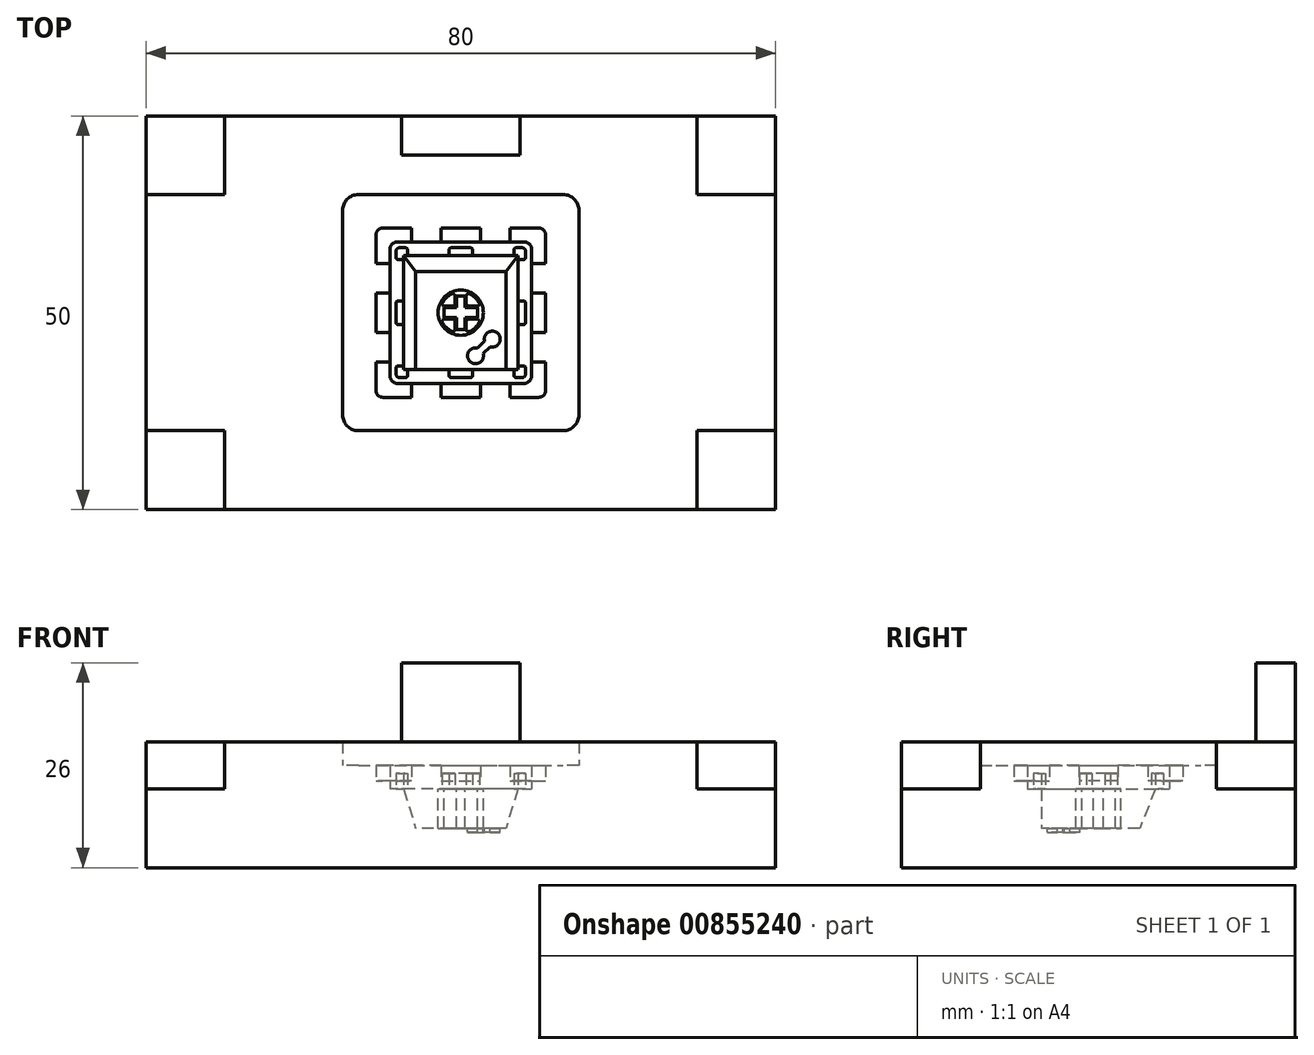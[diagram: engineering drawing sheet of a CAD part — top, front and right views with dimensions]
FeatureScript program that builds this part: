
annotation { "Feature Type Name" : "Feature", "Feature Type Description" : "" }
export const myFeature = defineFeature(function(context is Context, id is Id, definition is map)
    precondition{}
    {
        {
            var Q0;
            Q0=qCreatedBy(makeId("Top.planeOp"),FACE);
            var sketch = newSketch(context, id + "F0", { "sketchPlane" : qUnion([Q0])});
            skLineSegment(sketch, "E0", {"start": v(40, -25) * mm, "end": v(-40, -25) * mm});
            skLineSegment(sketch, "E1", {"start": v(-40, -25) * mm, "end": v(-40, 25) * mm});
            skLineSegment(sketch, "E2", {"start": v(-40, 25) * mm, "end": v(40, 25) * mm});
            skLineSegment(sketch, "E3", {"start": v(40, 25) * mm, "end": v(40, -25) * mm});
            skSolve(sketch);
        }
        {
            var Q0;
            Q0=makeQuery(id+"F0.imprint","IMPRINT",FACE,{"disambiguationData":[TD([[makeQuery(id+"F0.imprint","IMPRINT",EDGE,{"derivedFrom":sQuery(id+"F0.wireOp",EDGE,"E0")}),-1.0]])]});
            extrude(context, id + "F1", {"entities" : qUnion([Q0]), "depth" : 10 * mm, "offsetDistance" : 25 * mm});
        }
        {
            var Q0;
            Q0=qCreatedBy(makeId("Top.planeOp"),FACE);
            var sketch = newSketch(context, id + "F2", { "sketchPlane" : qUnion([Q0])});
            skCircle(sketch, "E4", {"center": v(0, 0) * mm, "radius": 2.87 * mm});
            skLineSegment(sketch, "E5", {"start": v(2.12, -0.64) * mm, "end": v(0.54, -0.64) * mm});
            skLineSegment(sketch, "E6", {"start": v(-2.12, 0.64) * mm, "end": v(-0.54, 0.64) * mm});
            skLineSegment(sketch, "E7", {"start": v(-0.54, 2.13) * mm, "end": v(-0.54, 0.64) * mm});
            skLineSegment(sketch, "E8", {"start": v(0.54, 2.12) * mm, "end": v(0.54, 0.64) * mm});
            skLineSegment(sketch, "E9.trimOffspring", {"start": v(-0.54, -0.64) * mm, "end": v(-0.54, -2.12) * mm});
            skLineSegment(sketch, "E10.trimOffspring", {"start": v(0.54, -0.64) * mm, "end": v(0.54, -2.13) * mm});
            skLineSegment(sketch, "E11.trimOffspring", {"start": v(0.54, 0.64) * mm, "end": v(2.12, 0.64) * mm});
            skLineSegment(sketch, "E12.trimOffspring", {"start": v(-0.54, -0.64) * mm, "end": v(-2.13, -0.64) * mm});
            skLineSegment(sketch, "E13", {"start": v(-7.25, -7.25) * mm, "end": v(7.25, -7.25) * mm});
            skLineSegment(sketch, "E14", {"start": v(7.25, -7.25) * mm, "end": v(7.25, 7.25) * mm});
            skLineSegment(sketch, "E15", {"start": v(7.25, 7.25) * mm, "end": v(-7.25, 7.25) * mm});
            skLineSegment(sketch, "E16", {"start": v(-5.75, -7.25) * mm, "end": v(5.75, -7.25) * mm});
            skLineSegment(sketch, "E17", {"start": v(5.75, 5.25) * mm, "end": v(-5.75, 5.25) * mm});
            skLineSegment(sketch, "E18", {"start": v(-7.25, 7.25) * mm, "end": v(-7.25, -7.25) * mm});
            skLineSegment(sketch, "E19", {"start": v(-5.75, 5.25) * mm, "end": v(-5.75, -7.25) * mm});
            skLineSegment(sketch, "E20", {"start": v(5.75, 5.25) * mm, "end": v(5.75, -7.25) * mm});
            skLineSegment(sketch, "E21", {"start": v(-2.13, 0.64) * mm, "end": v(-2.13, -0.64) * mm});
            skLineSegment(sketch, "E22", {"start": v(-0.54, 2.13) * mm, "end": v(0.54, 2.12) * mm});
            skLineSegment(sketch, "E23", {"start": v(2.13, 0.64) * mm, "end": v(2.12, -0.64) * mm});
            skLineSegment(sketch, "E24", {"start": v(-0.54, -2.12) * mm, "end": v(0.54, -2.13) * mm});
            skSolve(sketch);
        }
        {
            var Q0;
            Q0=qCreatedBy(makeId("Top.planeOp"),FACE);
            cPlane(context, id + "F3", {"entities" : qUnion([Q0]), "cplaneType" : CPlaneType.OFFSET, "offset" : 5 * mm, "width" : 150 * mm, "height" : 150 * mm});
        }
        {
            var Q0;
            Q0=qCreatedBy(id+"F3.planeOp",FACE);
            var sketch = newSketch(context, id + "F4", { "sketchPlane" : qUnion([Q0])});
            skLineSegment(sketch, "E25.0", {"start": v(5.75, 5.25) * mm, "end": v(-5.75, 5.25) * mm});
            skLineSegment(sketch, "E25.1", {"start": v(-5.75, 5.25) * mm, "end": v(-5.75, -7.25) * mm});
            skLineSegment(sketch, "E25.2", {"start": v(-5.75, -7.25) * mm, "end": v(5.75, -7.25) * mm});
            skLineSegment(sketch, "E25.3", {"start": v(5.75, 5.25) * mm, "end": v(5.75, -7.25) * mm});
            skSolve(sketch);
        }
        {
            var Q0;
            Q0=qCreatedBy(makeId("Top.planeOp"),FACE);
            var sketch = newSketch(context, id + "F5", { "sketchPlane" : qUnion([Q0])});
            skLineSegment(sketch, "E26.0", {"start": v(7.25, 7.25) * mm, "end": v(-7.25, 7.25) * mm});
            skLineSegment(sketch, "E26.1", {"start": v(-7.25, 7.25) * mm, "end": v(-7.25, -7.25) * mm});
            skLineSegment(sketch, "E26.2", {"start": v(-7.25, -7.25) * mm, "end": v(7.25, -7.25) * mm});
            skLineSegment(sketch, "E26.3", {"start": v(7.25, -7.25) * mm, "end": v(7.25, 7.25) * mm});
            skSolve(sketch);
        }
        {
            var Q0;
            Q0 = qSketchRegion(id + "F5", true);
            var Q1;
            Q1=makeQuery(id+"F4.imprint","IMPRINT",FACE,{"disambiguationData":[TD([[makeQuery(id+"F4.imprint","IMPRINT",EDGE,{"derivedFrom":sQuery(id+"F4.wireOp",EDGE,"E25.0")}),1.0]])]});
            loft(context, id + "F6", {"operationType" : NewBodyOperationType.REMOVE, "sheetProfilesArray" : [{ "sheetProfileEntities" : qUnion([Q0]) }, { "sheetProfileEntities" : qUnion([Q1]) }]});
        }
        {
            var Q0;
            Q0=makeQuery(id+"F2.imprint","IMPRINT",FACE,{"disambiguationData":[TD([[makeQuery(id+"F2.imprint","IMPRINT",EDGE,{"derivedFrom":sQuery(id+"F2.wireOp",EDGE,"E4")}),1.0]])]});
            extrude(context, id + "F7", {"entities" : qUnion([Q0]), "operationType" : NewBodyOperationType.ADD, "depth" : 5 * mm, "offsetDistance" : 25 * mm});
        }
        {
            var Q0;
            Q0=makeQuery(id+"F0.imprint","IMPRINT",FACE,{"disambiguationData":[TD([[makeQuery(id+"F0.imprint","IMPRINT",EDGE,{"derivedFrom":sQuery(id+"F0.wireOp",EDGE,"E0")}),-1.0]])]});
            var sketch = newSketch(context, id + "F8", { "sketchPlane" : qUnion([Q0])});
            skLineSegment(sketch, "E27", {"start": v(8, 9) * mm, "end": v(-8, 9) * mm});
            skLineSegment(sketch, "E28", {"start": v(-9, 8) * mm, "end": v(-9, -8) * mm});
            skLineSegment(sketch, "E29", {"start": v(-8, -9) * mm, "end": v(8, -9) * mm});
            skLineSegment(sketch, "E30", {"start": v(9, -8) * mm, "end": v(9, 8) * mm});
            skLineSegment(sketch, "E31", {"start": v(13, -15) * mm, "end": v(-13, -15) * mm});
            skLineSegment(sketch, "E32", {"start": v(-15, -13) * mm, "end": v(-15, 13) * mm});
            skLineSegment(sketch, "E33", {"start": v(-13, 15) * mm, "end": v(13, 15) * mm});
            skLineSegment(sketch, "E34", {"start": v(15, 13) * mm, "end": v(15, -13) * mm});
            skPoint(sketch, "E35.visualSharp", {"position": v(-15, -15) * mm});
            skArc(sketch, "E35.filletArc", {"start": v(-15, -13) * mm, "mid": v(-14.41, -14.41) * mm, "end": v(-13, -15) * mm});
            skPoint(sketch, "E36.visualSharp", {"position": v(15, -15) * mm});
            skArc(sketch, "E36.filletArc", {"start": v(13, -15) * mm, "mid": v(14.41, -14.41) * mm, "end": v(15, -13) * mm});
            skPoint(sketch, "E37.visualSharp", {"position": v(15, 15) * mm});
            skArc(sketch, "E37.filletArc", {"start": v(15, 13) * mm, "mid": v(14.41, 14.41) * mm, "end": v(13, 15) * mm});
            skPoint(sketch, "E38.visualSharp", {"position": v(-15, 15) * mm});
            skArc(sketch, "E38.filletArc", {"start": v(-13, 15) * mm, "mid": v(-14.41, 14.41) * mm, "end": v(-15, 13) * mm});
            skLineSegment(sketch, "E39", {"start": v(-7.5, 20) * mm, "end": v(-7.5, 25) * mm});
            skLineSegment(sketch, "E40", {"start": v(-7.5, 25) * mm, "end": v(7.5, 25) * mm});
            skLineSegment(sketch, "E41", {"start": v(7.5, 25) * mm, "end": v(7.5, 20) * mm});
            skLineSegment(sketch, "E42", {"start": v(-7.5, 20) * mm, "end": v(7.5, 20) * mm});
            skLineSegment(sketch, "E43.0", {"start": v(-40, -25) * mm, "end": v(-40, 25) * mm});
            skLineSegment(sketch, "E43.1", {"start": v(40, -25) * mm, "end": v(-40, -25) * mm});
            skLineSegment(sketch, "E43.2", {"start": v(40, 25) * mm, "end": v(40, -25) * mm});
            skLineSegment(sketch, "E43.3", {"start": v(-40, 25) * mm, "end": v(40, 25) * mm});
            skLineSegment(sketch, "E44", {"start": v(-40, -25) * mm, "end": v(-40, -15) * mm});
            skLineSegment(sketch, "E45", {"start": v(-40, -15) * mm, "end": v(-30, -15) * mm});
            skLineSegment(sketch, "E46", {"start": v(-30, -15) * mm, "end": v(-30, -25) * mm});
            skLineSegment(sketch, "E47", {"start": v(-30, -25) * mm, "end": v(-40, -25) * mm});
            skLineSegment(sketch, "E48", {"start": v(40, -25) * mm, "end": v(30, -25) * mm});
            skLineSegment(sketch, "E49", {"start": v(30, -25) * mm, "end": v(30, -15) * mm});
            skLineSegment(sketch, "E50", {"start": v(30, -15) * mm, "end": v(40, -15) * mm});
            skLineSegment(sketch, "E51", {"start": v(40, -15) * mm, "end": v(40, -25) * mm});
            skLineSegment(sketch, "E52", {"start": v(-40, 25) * mm, "end": v(-40, 15) * mm});
            skLineSegment(sketch, "E53", {"start": v(-40, 15) * mm, "end": v(-30, 15) * mm});
            skLineSegment(sketch, "E54", {"start": v(-30, 15) * mm, "end": v(-30, 25) * mm});
            skLineSegment(sketch, "E55", {"start": v(-30, 25) * mm, "end": v(-40, 25) * mm});
            skLineSegment(sketch, "E56", {"start": v(40, 25) * mm, "end": v(40, 15) * mm});
            skLineSegment(sketch, "E57", {"start": v(40, 15) * mm, "end": v(30, 15) * mm});
            skLineSegment(sketch, "E58", {"start": v(30, 15) * mm, "end": v(30, 25) * mm});
            skLineSegment(sketch, "E59", {"start": v(30, 25) * mm, "end": v(40, 25) * mm});
            skPoint(sketch, "E60.visualSharp", {"position": v(-9, 9) * mm});
            skArc(sketch, "E60.filletArc", {"start": v(-8, 9) * mm, "mid": v(-8.7, 8.7) * mm, "end": v(-9, 8) * mm});
            skPoint(sketch, "E61.visualSharp", {"position": v(9, 9) * mm});
            skArc(sketch, "E61.filletArc", {"start": v(9, 8) * mm, "mid": v(8.7, 8.7) * mm, "end": v(8, 9) * mm});
            skPoint(sketch, "E62.visualSharp", {"position": v(9, -9) * mm});
            skArc(sketch, "E62.filletArc", {"start": v(8, -9) * mm, "mid": v(8.7, -8.7) * mm, "end": v(9, -8) * mm});
            skPoint(sketch, "E63.visualSharp", {"position": v(-9, -9) * mm});
            skArc(sketch, "E63.filletArc", {"start": v(-9, -8) * mm, "mid": v(-8.7, -8.7) * mm, "end": v(-8, -9) * mm});
            skSolve(sketch);
        }
        {
            var Q0;
            Q0=makeQuery(id+"F8.imprint","IMPRINT",FACE,{"disambiguationData":[TD([[makeQuery(id+"F8.imprint","IMPRINT",EDGE,{"derivedFrom":sQuery(id+"F8.wireOp",EDGE,"E27")}),-1.0]])]});
            var Q1;
            Q1=makeQuery(id+"F8.imprint","IMPRINT",FACE,{"disambiguationData":[TD([[makeQuery(id+"F8.imprint","IMPRINT",EDGE,{"derivedFrom":sQuery(id+"F8.wireOp",EDGE,"E48")}),-1.0]])]});
            var Q2;
            Q2=makeQuery(id+"F8.imprint","IMPRINT",FACE,{"disambiguationData":[TD([[makeQuery(id+"F8.imprint","IMPRINT",EDGE,{"derivedFrom":sQuery(id+"F8.wireOp",EDGE,"E56")}),-1.0]])]});
            var Q3;
            Q3=makeQuery(id+"F8.imprint","IMPRINT",FACE,{"disambiguationData":[TD([[makeQuery(id+"F8.imprint","IMPRINT",EDGE,{"derivedFrom":sQuery(id+"F8.wireOp",EDGE,"E31")}),1.0]])]});
            var Q4;
            {var subQ0=sQuery(id+"F8.wireOp",EDGE,"E39");Q4=makeQuery(id+"F8.imprint","IMPRINT",FACE,{"disambiguationData":[TD([[makeQuery(id+"F8.imprint","IMPRINT",EDGE,{"derivedFrom":subQ0}),-1.0]])]});}
            var Q5;
            Q5=makeQuery(id+"F8.imprint","IMPRINT",FACE,{"disambiguationData":[TD([[makeQuery(id+"F8.imprint","IMPRINT",EDGE,{"derivedFrom":sQuery(id+"F8.wireOp",EDGE,"E52")}),-1.0]])]});
            var Q6;
            Q6=makeQuery(id+"F8.imprint","IMPRINT",FACE,{"disambiguationData":[TD([[makeQuery(id+"F8.imprint","IMPRINT",EDGE,{"derivedFrom":sQuery(id+"F8.wireOp",EDGE,"E44")}),-1.0]])]});
            extrude(context, id + "F9", {"entities" : qUnion([Q0, Q1, Q2, Q3, Q4, Q5, Q6]), "operationType" : NewBodyOperationType.ADD, "oppositeDirection" : true, "depth" : 3 * mm, "offsetDistance" : 25 * mm});
        }
        {
            var Q0;
            Q0=makeQuery(id+"F8.imprint","IMPRINT",FACE,{"disambiguationData":[TD([[makeQuery(id+"F8.imprint","IMPRINT",EDGE,{"derivedFrom":sQuery(id+"F8.wireOp",EDGE,"E31")}),1.0]])]});
            var Q1;
            Q1=makeQuery(id+"F8.imprint","IMPRINT",FACE,{"disambiguationData":[TD([[makeQuery(id+"F8.imprint","IMPRINT",EDGE,{"derivedFrom":sQuery(id+"F8.wireOp",EDGE,"E48")}),-1.0]])]});
            var Q2;
            Q2=makeQuery(id+"F8.imprint","IMPRINT",FACE,{"disambiguationData":[TD([[makeQuery(id+"F8.imprint","IMPRINT",EDGE,{"derivedFrom":sQuery(id+"F8.wireOp",EDGE,"E56")}),-1.0]])]});
            var Q3;
            Q3=makeQuery(id+"F8.imprint","IMPRINT",FACE,{"disambiguationData":[TD([[makeQuery(id+"F8.imprint","IMPRINT",EDGE,{"derivedFrom":sQuery(id+"F8.wireOp",EDGE,"E52")}),-1.0]])]});
            var Q4;
            {var subQ0=sQuery(id+"F8.wireOp",EDGE,"E39");Q4=makeQuery(id+"F8.imprint","IMPRINT",FACE,{"disambiguationData":[TD([[makeQuery(id+"F8.imprint","IMPRINT",EDGE,{"derivedFrom":subQ0}),-1.0]])]});}
            var Q5;
            Q5=makeQuery(id+"F8.imprint","IMPRINT",FACE,{"disambiguationData":[TD([[makeQuery(id+"F8.imprint","IMPRINT",EDGE,{"derivedFrom":sQuery(id+"F8.wireOp",EDGE,"E44")}),-1.0]])]});
            extrude(context, id + "F10", {"entities" : qUnion([Q0, Q1, Q2, Q3, Q4, Q5]), "operationType" : NewBodyOperationType.ADD, "oppositeDirection" : true, "depth" : 6 * mm, "offsetDistance" : 25 * mm});
        }
        {
            var Q0;
            Q0=qCreatedBy(id+"F3.planeOp",FACE);
            var sketch = newSketch(context, id + "F11", { "sketchPlane" : qUnion([Q0])});
            skFitSpline(sketch, "E64", {"points": [v(-4, -5.85) * mm, v(-3.95, -6) * mm, v(-3.67, -6.34) * mm, v(-3.46, -6.52) * mm, v(-3.17, -6.5) * mm, v(-2.96, -6.4) * mm, v(-2.55, -6.17) * mm, v(-2.35, -5.86) * mm, v(-2.28, -5.34) * mm, v(-2.43, -4.96) * mm, v(-2.58, -4.76) * mm, v(-2.67, -4.7) * mm, v(-2.69, -4.64) * mm, v(-2.62, -4.54) * mm, v(-2.33, -4.48) * mm, v(-2.15, -4.64) * mm, v(-1.78, -4.82) * mm, v(-1.4, -4.65) * mm, v(-1.35, -4.47) * mm, v(-1.26, -4.08) * mm, v(-1.33, -3.65) * mm, v(-1.64, -3.19) * mm, v(-2.13, -2.87) * mm, v(-3.35, -2.7) * mm, v(-4.24, -2.79) * mm, v(-4.63, -3.02) * mm, v(-4.9, -3.3) * mm, v(-4.95, -3.8) * mm, v(-4.7, -4.22) * mm, v(-4.4, -4.5) * mm, v(-4.15, -4.7) * mm, v(-4.06, -4.83) * mm, v(-4.1, -5.06) * mm, v(-4.22, -5.17) * mm, v(-4.39, -5.14) * mm, v(-4.57, -5.22) * mm, v(-4.46, -5.43) * mm, v(-4.55, -5.55) * mm, v(-4.61, -5.66) * mm, v(-4.6, -5.86) * mm, v(-4.48, -5.95) * mm, v(-4.31, -5.9) * mm, v(-4.16, -5.85) * mm, v(-4, -5.85) * mm]});
            skSolve(sketch);
        }
        {
            var Q0;
            Q0=makeQuery(id+"F10.opExtrude","CAP_FACE",FACE,{"disambiguationData":[OSD([sQuery(id+"F8.wireOp",EDGE,"E31"),sQuery(id+"F8.wireOp",EDGE,"E32"),sQuery(id+"F8.wireOp",EDGE,"E33"),sQuery(id+"F8.wireOp",EDGE,"E34"),sQuery(id+"F8.wireOp",EDGE,"E35.filletArc"),sQuery(id+"F8.wireOp",EDGE,"E36.filletArc"),sQuery(id+"F8.wireOp",EDGE,"E37.filletArc"),sQuery(id+"F8.wireOp",EDGE,"E38.filletArc"),sQuery(id+"F8.wireOp",EDGE,"E43.0"),sQuery(id+"F8.wireOp",EDGE,"E43.1"),sQuery(id+"F8.wireOp",EDGE,"E43.2"),sQuery(id+"F8.wireOp",EDGE,"E43.3"),sQuery(id+"F8.wireOp",EDGE,"E44"),sQuery(id+"F8.wireOp",EDGE,"E47"),sQuery(id+"F8.wireOp",EDGE,"E48"),sQuery(id+"F8.wireOp",EDGE,"E51"),sQuery(id+"F8.wireOp",EDGE,"E52"),sQuery(id+"F8.wireOp",EDGE,"E55"),sQuery(id+"F8.wireOp",EDGE,"E56"),sQuery(id+"F8.wireOp",EDGE,"E59")])],"isStart":false});
            var sketch = newSketch(context, id + "F12", { "sketchPlane" : qUnion([Q0])});
            skLineSegment(sketch, "E65.0", {"start": v(40, 25) * mm, "end": v(-40, 25) * mm});
            skLineSegment(sketch, "E65.1", {"start": v(40, -25) * mm, "end": v(40, 25) * mm});
            skLineSegment(sketch, "E65.2", {"start": v(-40, -25) * mm, "end": v(40, -25) * mm});
            skLineSegment(sketch, "E65.3", {"start": v(-40, 25) * mm, "end": v(-40, -25) * mm});
            skLineSegment(sketch, "E66", {"start": v(-40, -25) * mm, "end": v(-40, -20) * mm});
            skLineSegment(sketch, "E67", {"start": v(-40, -20) * mm, "end": v(-35, -20) * mm});
            skLineSegment(sketch, "E68", {"start": v(-35, -20) * mm, "end": v(-35, -25) * mm});
            skLineSegment(sketch, "E69", {"start": v(-35, -25) * mm, "end": v(-40, -25) * mm});
            skLineSegment(sketch, "E70", {"start": v(40, -25) * mm, "end": v(40, -20) * mm});
            skLineSegment(sketch, "E71", {"start": v(40, -20) * mm, "end": v(35, -20) * mm});
            skLineSegment(sketch, "E72", {"start": v(35, -20) * mm, "end": v(35, -25) * mm});
            skLineSegment(sketch, "E73", {"start": v(35, -25) * mm, "end": v(40, -25) * mm});
            skLineSegment(sketch, "E74", {"start": v(40, 25) * mm, "end": v(35, 25) * mm});
            skLineSegment(sketch, "E75", {"start": v(35, 25) * mm, "end": v(35, 20) * mm});
            skLineSegment(sketch, "E76", {"start": v(35, 20) * mm, "end": v(40, 20) * mm});
            skLineSegment(sketch, "E77", {"start": v(40, 20) * mm, "end": v(40, 25) * mm});
            skLineSegment(sketch, "E78", {"start": v(-40, 25) * mm, "end": v(-35, 25) * mm});
            skLineSegment(sketch, "E79", {"start": v(-35, 25) * mm, "end": v(-35, 20) * mm});
            skLineSegment(sketch, "E80", {"start": v(-35, 20) * mm, "end": v(-40, 20) * mm});
            skLineSegment(sketch, "E81", {"start": v(-40, 20) * mm, "end": v(-40, 25) * mm});
            skLineSegment(sketch, "E82", {"start": v(0, -20) * mm, "end": v(7.5, -20) * mm});
            skLineSegment(sketch, "E83", {"start": v(7.5, -20) * mm, "end": v(7.5, -25) * mm});
            skLineSegment(sketch, "E84", {"start": v(7.5, -25) * mm, "end": v(-7.5, -25) * mm});
            skLineSegment(sketch, "E85", {"start": v(-7.5, -25) * mm, "end": v(-7.5, -20) * mm});
            skLineSegment(sketch, "E86", {"start": v(-7.5, -20) * mm, "end": v(0, -20) * mm});
            skSolve(sketch);
        }
        {
            var Q0;
            Q0=makeQuery(id+"F12.imprint","IMPRINT",FACE,{"disambiguationData":[TD([[makeQuery(id+"F12.imprint","IMPRINT",EDGE,{"derivedFrom":sQuery(id+"F12.wireOp",EDGE,"E78")}),1.0]])]});
            var Q1;
            Q1=makeQuery(id+"F12.imprint","IMPRINT",FACE,{"disambiguationData":[TD([[makeQuery(id+"F12.imprint","IMPRINT",EDGE,{"derivedFrom":sQuery(id+"F12.wireOp",EDGE,"E74")}),1.0]])]});
            var Q2;
            Q2=makeQuery(id+"F12.imprint","IMPRINT",FACE,{"disambiguationData":[TD([[makeQuery(id+"F12.imprint","IMPRINT",EDGE,{"derivedFrom":sQuery(id+"F12.wireOp",EDGE,"E70")}),1.0]])]});
            var Q3;
            Q3=makeQuery(id+"F12.imprint","IMPRINT",FACE,{"disambiguationData":[TD([[makeQuery(id+"F12.imprint","IMPRINT",EDGE,{"derivedFrom":sQuery(id+"F12.wireOp",EDGE,"E82")}),-1.0]])]});
            var Q4;
            Q4=makeQuery(id+"F12.imprint","IMPRINT",FACE,{"disambiguationData":[TD([[makeQuery(id+"F12.imprint","IMPRINT",EDGE,{"derivedFrom":sQuery(id+"F12.wireOp",EDGE,"E66")}),1.0]])]});
            extrude(context, id + "F13", {"entities" : qUnion([Q0, Q1, Q2, Q3, Q4]), "operationType" : NewBodyOperationType.ADD, "depth" : 10 * mm, "offsetDistance" : 25 * mm});
        }
        {
            var Q0;
            Q0=makeQuery(id+"F1.opExtrude","CAP_FACE",FACE,{"disambiguationData":[OSD([sQuery(id+"F0.wireOp",EDGE,"E0"),sQuery(id+"F0.wireOp",EDGE,"E1"),sQuery(id+"F0.wireOp",EDGE,"E2"),sQuery(id+"F0.wireOp",EDGE,"E3")])],"isStart":true});
            var sketch = newSketch(context, id + "F14", { "sketchPlane" : qUnion([Q0])});
            skArc(sketch, "E87", {"start": v(-2.32, -1.27) * mm, "mid": v(-1.81, -1.93) * mm, "end": v(-1.12, -2.4) * mm});
            skLineSegment(sketch, "E88", {"start": v(-0.7, -2.13) * mm, "end": v(-0.7, -1.13) * mm});
            skLineSegment(sketch, "E89", {"start": v(0.73, 2.11) * mm, "end": v(0.73, 1.11) * mm});
            skLineSegment(sketch, "E90", {"start": v(2.07, 0.81) * mm, "end": v(1.03, 0.81) * mm});
            skLineSegment(sketch, "E91", {"start": v(2.06, -0.83) * mm, "end": v(1.03, -0.83) * mm});
            skLineSegment(sketch, "E92.trimOffspring", {"start": v(-1, 0.81) * mm, "end": v(-2.07, 0.81) * mm});
            skLineSegment(sketch, "E93.trimOffspring", {"start": v(-0.7, 1.11) * mm, "end": v(-0.7, 2.13) * mm});
            skLineSegment(sketch, "E94.trimOffspring", {"start": v(-1, -0.83) * mm, "end": v(-2.06, -0.83) * mm});
            skLineSegment(sketch, "E95.trimOffspring", {"start": v(0.73, -1.13) * mm, "end": v(0.73, -2.11) * mm});
            skArc(sketch, "E96.trimOffspring", {"start": v(2.33, 1.25) * mm, "mid": v(1.84, 1.9) * mm, "end": v(1.16, 2.38) * mm});
            skArc(sketch, "E97.trimOffspring", {"start": v(-1.12, 2.4) * mm, "mid": v(-1.82, 1.92) * mm, "end": v(-2.33, 1.25) * mm});
            skArc(sketch, "E98.trimOffspring", {"start": v(1.16, -2.38) * mm, "mid": v(1.83, -1.92) * mm, "end": v(2.32, -1.27) * mm});
            skLineSegment(sketch, "E99", {"start": v(1.2, 7.25) * mm, "end": v(-1.2, 7.25) * mm});
            skLineSegment(sketch, "E100", {"start": v(-1.5, 7.55) * mm, "end": v(-1.5, 7.95) * mm});
            skLineSegment(sketch, "E101", {"start": v(-1.2, 8.25) * mm, "end": v(1.2, 8.25) * mm});
            skLineSegment(sketch, "E102", {"start": v(1.5, 7.95) * mm, "end": v(1.5, 7.55) * mm});
            skLineSegment(sketch, "E103.MirrorCS", {"start": v(1.5, -7.95) * mm, "end": v(1.5, -7.55) * mm});
            skLineSegment(sketch, "E104.MirrorCS", {"start": v(-1.2, -8.25) * mm, "end": v(1.2, -8.25) * mm});
            skLineSegment(sketch, "E105.MirrorCS", {"start": v(1.2, -7.25) * mm, "end": v(-1.2, -7.25) * mm});
            skLineSegment(sketch, "E106.MirrorCS", {"start": v(-1.5, -7.55) * mm, "end": v(-1.5, -7.95) * mm});
            skLineSegment(sketch, "E107", {"start": v(-7.25, 1.2) * mm, "end": v(-7.25, -1.2) * mm});
            skLineSegment(sketch, "E108", {"start": v(-7.55, -1.5) * mm, "end": v(-7.95, -1.5) * mm});
            skLineSegment(sketch, "E109", {"start": v(-8.25, -1.2) * mm, "end": v(-8.25, 1.2) * mm});
            skLineSegment(sketch, "E110", {"start": v(-7.95, 1.5) * mm, "end": v(-7.55, 1.5) * mm});
            skLineSegment(sketch, "E111.MirrorCS", {"start": v(8.25, -1.2) * mm, "end": v(8.25, 1.2) * mm});
            skLineSegment(sketch, "E112.MirrorCS", {"start": v(7.55, -1.5) * mm, "end": v(7.95, -1.5) * mm});
            skLineSegment(sketch, "E113.MirrorCS", {"start": v(7.95, 1.5) * mm, "end": v(7.55, 1.5) * mm});
            skLineSegment(sketch, "E114.MirrorCS", {"start": v(7.25, 1.2) * mm, "end": v(7.25, -1.2) * mm});
            skLineSegment(sketch, "E115", {"start": v(8.25, -7.25) * mm, "end": v(8.25, -7.75) * mm});
            skLineSegment(sketch, "E116", {"start": v(7.75, -8.25) * mm, "end": v(7.25, -8.25) * mm});
            skLineSegment(sketch, "E117", {"start": v(7.25, -8.25) * mm, "end": v(7.05, -8.25) * mm});
            skLineSegment(sketch, "E118", {"start": v(6.75, -7.95) * mm, "end": v(6.75, -7.55) * mm});
            skLineSegment(sketch, "E119", {"start": v(7.05, -7.25) * mm, "end": v(7.25, -7.25) * mm});
            skLineSegment(sketch, "E120", {"start": v(8.25, -7.25) * mm, "end": v(8.25, -7.05) * mm});
            skLineSegment(sketch, "E121", {"start": v(7.95, -6.75) * mm, "end": v(7.55, -6.75) * mm});
            skLineSegment(sketch, "E122", {"start": v(7.25, -7.05) * mm, "end": v(7.25, -7.25) * mm});
            skPoint(sketch, "E123.visualSharp", {"position": v(8.75, -8.75) * mm});
            skArc(sketch, "E123.filletArc", {"start": v(7.75, -8.25) * mm, "mid": v(8.1, -8.1) * mm, "end": v(8.25, -7.75) * mm});
            skLineSegment(sketch, "E124.MirrorCS", {"start": v(-7.05, -7.25) * mm, "end": v(-7.25, -7.25) * mm});
            skLineSegment(sketch, "E125.MirrorCS", {"start": v(-7.25, -7.05) * mm, "end": v(-7.25, -7.25) * mm});
            skLineSegment(sketch, "E126.MirrorCS", {"start": v(-7.95, -6.75) * mm, "end": v(-7.55, -6.75) * mm});
            skLineSegment(sketch, "E127.MirrorCS", {"start": v(-8.25, -7.25) * mm, "end": v(-8.25, -7.05) * mm});
            skLineSegment(sketch, "E128.MirrorCS", {"start": v(-8.25, -7.25) * mm, "end": v(-8.25, -7.75) * mm});
            skArc(sketch, "E129.MirrorCS", {"start": v(-7.75, -8.25) * mm, "mid": v(-8.1, -8.1) * mm, "end": v(-8.25, -7.75) * mm});
            skLineSegment(sketch, "E130.MirrorCS", {"start": v(-7.75, -8.25) * mm, "end": v(-7.25, -8.25) * mm});
            skLineSegment(sketch, "E131.MirrorCS", {"start": v(-6.75, -7.95) * mm, "end": v(-6.75, -7.55) * mm});
            skLineSegment(sketch, "E132.MirrorCS", {"start": v(-7.25, -8.25) * mm, "end": v(-7.05, -8.25) * mm});
            skLineSegment(sketch, "E133.MirrorCS", {"start": v(7.05, 7.25) * mm, "end": v(7.25, 7.25) * mm});
            skLineSegment(sketch, "E134.MirrorCS", {"start": v(7.25, 7.05) * mm, "end": v(7.25, 7.25) * mm});
            skLineSegment(sketch, "E135.MirrorCS", {"start": v(7.95, 6.75) * mm, "end": v(7.55, 6.75) * mm});
            skLineSegment(sketch, "E136.MirrorCS", {"start": v(8.25, 7.25) * mm, "end": v(8.25, 7.05) * mm});
            skLineSegment(sketch, "E137.MirrorCS", {"start": v(8.25, 7.25) * mm, "end": v(8.25, 7.75) * mm});
            skArc(sketch, "E138.MirrorCS", {"start": v(7.75, 8.25) * mm, "mid": v(8.1, 8.1) * mm, "end": v(8.25, 7.75) * mm});
            skLineSegment(sketch, "E139.MirrorCS", {"start": v(7.75, 8.25) * mm, "end": v(7.25, 8.25) * mm});
            skLineSegment(sketch, "E140.MirrorCS", {"start": v(7.25, 8.25) * mm, "end": v(7.05, 8.25) * mm});
            skLineSegment(sketch, "E141.MirrorCS", {"start": v(6.75, 7.95) * mm, "end": v(6.75, 7.55) * mm});
            skLineSegment(sketch, "E142.MirrorCS", {"start": v(-7.05, 7.25) * mm, "end": v(-7.25, 7.25) * mm});
            skLineSegment(sketch, "E143.MirrorCS", {"start": v(-7.25, 7.05) * mm, "end": v(-7.25, 7.25) * mm});
            skLineSegment(sketch, "E144.MirrorCS", {"start": v(-7.95, 6.75) * mm, "end": v(-7.55, 6.75) * mm});
            skLineSegment(sketch, "E145.MirrorCS", {"start": v(-8.25, 7.25) * mm, "end": v(-8.25, 7.05) * mm});
            skLineSegment(sketch, "E146.MirrorCS", {"start": v(-8.25, 7.25) * mm, "end": v(-8.25, 7.75) * mm});
            skArc(sketch, "E147.MirrorCS", {"start": v(-7.75, 8.25) * mm, "mid": v(-8.1, 8.1) * mm, "end": v(-8.25, 7.75) * mm});
            skLineSegment(sketch, "E148.MirrorCS", {"start": v(-7.75, 8.25) * mm, "end": v(-7.25, 8.25) * mm});
            skLineSegment(sketch, "E149.MirrorCS", {"start": v(-6.75, 7.95) * mm, "end": v(-6.75, 7.55) * mm});
            skLineSegment(sketch, "E150.MirrorCS", {"start": v(-7.25, 8.25) * mm, "end": v(-7.05, 8.25) * mm});
            skPoint(sketch, "E151.orphan", {"position": v(8.75, 1.5) * mm});
            skPoint(sketch, "E152.orphan", {"position": v(8.75, -1.5) * mm});
            skPoint(sketch, "E153.orphan", {"position": v(8.75, -6.75) * mm});
            skPoint(sketch, "E154.orphan", {"position": v(6.75, -8.75) * mm});
            skPoint(sketch, "E155.orphan", {"position": v(1.5, -8.75) * mm});
            skPoint(sketch, "E156.orphan", {"position": v(-1.5, -8.75) * mm});
            skPoint(sketch, "E157.orphan", {"position": v(-6.75, -8.75) * mm});
            skPoint(sketch, "E158.orphan", {"position": v(-8.75, -6.75) * mm});
            skPoint(sketch, "E159.orphan", {"position": v(-8.75, -1.5) * mm});
            skPoint(sketch, "E160.orphan", {"position": v(-8.75, 1.5) * mm});
            skPoint(sketch, "E161.orphan", {"position": v(-8.75, 6.75) * mm});
            skPoint(sketch, "E162.orphan", {"position": v(-6.75, 8.75) * mm});
            skPoint(sketch, "E163.orphan", {"position": v(-1.5, 8.75) * mm});
            skPoint(sketch, "E164.orphan", {"position": v(1.5, 8.75) * mm});
            skPoint(sketch, "E165.orphan", {"position": v(6.75, 8.75) * mm});
            skPoint(sketch, "E166.orphan", {"position": v(8.75, 6.75) * mm});
            skPoint(sketch, "E167.visualSharp", {"position": v(8.25, -1.5) * mm});
            skArc(sketch, "E167.filletArc", {"start": v(7.95, -1.5) * mm, "mid": v(8.16, -1.41) * mm, "end": v(8.25, -1.2) * mm});
            skPoint(sketch, "E168.visualSharp", {"position": v(8.25, 1.5) * mm});
            skArc(sketch, "E168.filletArc", {"start": v(8.25, 1.2) * mm, "mid": v(8.16, 1.41) * mm, "end": v(7.95, 1.5) * mm});
            skPoint(sketch, "E169.visualSharp", {"position": v(7.25, 1.5) * mm});
            skArc(sketch, "E169.filletArc", {"start": v(7.55, 1.5) * mm, "mid": v(7.34, 1.41) * mm, "end": v(7.25, 1.2) * mm});
            skPoint(sketch, "E170.visualSharp", {"position": v(7.25, -1.5) * mm});
            skArc(sketch, "E170.filletArc", {"start": v(7.25, -1.2) * mm, "mid": v(7.34, -1.41) * mm, "end": v(7.55, -1.5) * mm});
            skPoint(sketch, "E171.visualSharp", {"position": v(1.5, 8.25) * mm});
            skArc(sketch, "E171.filletArc", {"start": v(1.5, 7.95) * mm, "mid": v(1.41, 8.16) * mm, "end": v(1.2, 8.25) * mm});
            skPoint(sketch, "E172.visualSharp", {"position": v(-1.5, 8.25) * mm});
            skArc(sketch, "E172.filletArc", {"start": v(-1.2, 8.25) * mm, "mid": v(-1.41, 8.16) * mm, "end": v(-1.5, 7.95) * mm});
            skPoint(sketch, "E173.visualSharp", {"position": v(-1.5, 7.25) * mm});
            skArc(sketch, "E173.filletArc", {"start": v(-1.5, 7.55) * mm, "mid": v(-1.41, 7.34) * mm, "end": v(-1.2, 7.25) * mm});
            skPoint(sketch, "E174.visualSharp", {"position": v(1.5, 7.25) * mm});
            skArc(sketch, "E174.filletArc", {"start": v(1.2, 7.25) * mm, "mid": v(1.41, 7.34) * mm, "end": v(1.5, 7.55) * mm});
            skPoint(sketch, "E175.visualSharp", {"position": v(6.75, 8.25) * mm});
            skArc(sketch, "E175.filletArc", {"start": v(7.05, 8.25) * mm, "mid": v(6.84, 8.16) * mm, "end": v(6.75, 7.95) * mm});
            skPoint(sketch, "E176.visualSharp", {"position": v(8.25, 6.75) * mm});
            skArc(sketch, "E176.filletArc", {"start": v(7.95, 6.75) * mm, "mid": v(8.16, 6.84) * mm, "end": v(8.25, 7.05) * mm});
            skPoint(sketch, "E177.visualSharp", {"position": v(7.25, 6.75) * mm});
            skArc(sketch, "E177.filletArc", {"start": v(7.25, 7.05) * mm, "mid": v(7.34, 6.84) * mm, "end": v(7.55, 6.75) * mm});
            skPoint(sketch, "E178.visualSharp", {"position": v(6.75, 7.25) * mm});
            skArc(sketch, "E178.filletArc", {"start": v(6.75, 7.55) * mm, "mid": v(6.84, 7.34) * mm, "end": v(7.05, 7.25) * mm});
            skPoint(sketch, "E179.visualSharp", {"position": v(-6.75, 8.25) * mm});
            skArc(sketch, "E179.filletArc", {"start": v(-6.75, 7.95) * mm, "mid": v(-6.84, 8.16) * mm, "end": v(-7.05, 8.25) * mm});
            skPoint(sketch, "E180.visualSharp", {"position": v(-6.75, 7.25) * mm});
            skArc(sketch, "E180.filletArc", {"start": v(-7.05, 7.25) * mm, "mid": v(-6.84, 7.34) * mm, "end": v(-6.75, 7.55) * mm});
            skPoint(sketch, "E181.visualSharp", {"position": v(-7.25, 6.75) * mm});
            skArc(sketch, "E181.filletArc", {"start": v(-7.55, 6.75) * mm, "mid": v(-7.34, 6.84) * mm, "end": v(-7.25, 7.05) * mm});
            skPoint(sketch, "E182.visualSharp", {"position": v(-8.25, 6.75) * mm});
            skArc(sketch, "E182.filletArc", {"start": v(-8.25, 7.05) * mm, "mid": v(-8.16, 6.84) * mm, "end": v(-7.95, 6.75) * mm});
            skPoint(sketch, "E183.visualSharp", {"position": v(-7.25, 1.5) * mm});
            skArc(sketch, "E183.filletArc", {"start": v(-7.25, 1.2) * mm, "mid": v(-7.34, 1.41) * mm, "end": v(-7.55, 1.5) * mm});
            skPoint(sketch, "E184.visualSharp", {"position": v(-8.25, 1.5) * mm});
            skArc(sketch, "E184.filletArc", {"start": v(-7.95, 1.5) * mm, "mid": v(-8.16, 1.41) * mm, "end": v(-8.25, 1.2) * mm});
            skPoint(sketch, "E185.visualSharp", {"position": v(-8.25, -1.5) * mm});
            skArc(sketch, "E185.filletArc", {"start": v(-8.25, -1.2) * mm, "mid": v(-8.16, -1.41) * mm, "end": v(-7.95, -1.5) * mm});
            skPoint(sketch, "E186.visualSharp", {"position": v(-7.25, -1.5) * mm});
            skArc(sketch, "E186.filletArc", {"start": v(-7.55, -1.5) * mm, "mid": v(-7.34, -1.41) * mm, "end": v(-7.25, -1.2) * mm});
            skPoint(sketch, "E187.visualSharp", {"position": v(-6.75, -8.25) * mm});
            skArc(sketch, "E187.filletArc", {"start": v(-7.05, -8.25) * mm, "mid": v(-6.84, -8.16) * mm, "end": v(-6.75, -7.95) * mm});
            skPoint(sketch, "E188.visualSharp", {"position": v(-6.75, -7.25) * mm});
            skArc(sketch, "E188.filletArc", {"start": v(-6.75, -7.55) * mm, "mid": v(-6.84, -7.34) * mm, "end": v(-7.05, -7.25) * mm});
            skPoint(sketch, "E189.visualSharp", {"position": v(-7.25, -6.75) * mm});
            skArc(sketch, "E189.filletArc", {"start": v(-7.25, -7.05) * mm, "mid": v(-7.34, -6.84) * mm, "end": v(-7.55, -6.75) * mm});
            skPoint(sketch, "E190.visualSharp", {"position": v(-8.25, -6.75) * mm});
            skArc(sketch, "E190.filletArc", {"start": v(-7.95, -6.75) * mm, "mid": v(-8.16, -6.84) * mm, "end": v(-8.25, -7.05) * mm});
            skPoint(sketch, "E191.visualSharp", {"position": v(-1.5, -8.25) * mm});
            skArc(sketch, "E191.filletArc", {"start": v(-1.5, -7.95) * mm, "mid": v(-1.41, -8.16) * mm, "end": v(-1.2, -8.25) * mm});
            skPoint(sketch, "E192.visualSharp", {"position": v(1.5, -8.25) * mm});
            skArc(sketch, "E192.filletArc", {"start": v(1.2, -8.25) * mm, "mid": v(1.41, -8.16) * mm, "end": v(1.5, -7.95) * mm});
            skPoint(sketch, "E193.visualSharp", {"position": v(1.5, -7.25) * mm});
            skArc(sketch, "E193.filletArc", {"start": v(1.5, -7.55) * mm, "mid": v(1.41, -7.34) * mm, "end": v(1.2, -7.25) * mm});
            skPoint(sketch, "E194.visualSharp", {"position": v(-1.5, -7.25) * mm});
            skArc(sketch, "E194.filletArc", {"start": v(-1.2, -7.25) * mm, "mid": v(-1.41, -7.34) * mm, "end": v(-1.5, -7.55) * mm});
            skPoint(sketch, "E195.visualSharp", {"position": v(6.75, -8.25) * mm});
            skArc(sketch, "E195.filletArc", {"start": v(6.75, -7.95) * mm, "mid": v(6.84, -8.16) * mm, "end": v(7.05, -8.25) * mm});
            skPoint(sketch, "E196.visualSharp", {"position": v(6.75, -7.25) * mm});
            skArc(sketch, "E196.filletArc", {"start": v(7.05, -7.25) * mm, "mid": v(6.84, -7.34) * mm, "end": v(6.75, -7.55) * mm});
            skPoint(sketch, "E197.visualSharp", {"position": v(7.25, -6.75) * mm});
            skArc(sketch, "E197.filletArc", {"start": v(7.55, -6.75) * mm, "mid": v(7.34, -6.84) * mm, "end": v(7.25, -7.05) * mm});
            skPoint(sketch, "E198.visualSharp", {"position": v(8.25, -6.75) * mm});
            skArc(sketch, "E198.filletArc", {"start": v(8.25, -7.05) * mm, "mid": v(8.16, -6.84) * mm, "end": v(7.95, -6.75) * mm});
            skPoint(sketch, "E199.visualSharp", {"position": v(0.73, -0.83) * mm});
            skArc(sketch, "E199.filletArc", {"start": v(1.03, -0.83) * mm, "mid": v(0.82, -0.92) * mm, "end": v(0.73, -1.13) * mm});
            skPoint(sketch, "E200.visualSharp", {"position": v(0.73, -2.55) * mm});
            skArc(sketch, "E200.filletArc", {"start": v(0.73, -2.11) * mm, "mid": v(0.87, -2.37) * mm, "end": v(1.16, -2.38) * mm});
            skPoint(sketch, "E201.visualSharp", {"position": v(2.52, -0.83) * mm});
            skArc(sketch, "E201.filletArc", {"start": v(2.32, -1.27) * mm, "mid": v(2.32, -0.98) * mm, "end": v(2.06, -0.83) * mm});
            skPoint(sketch, "E202.visualSharp", {"position": v(-0.7, -2.56) * mm});
            skArc(sketch, "E202.filletArc", {"start": v(-1.12, -2.4) * mm, "mid": v(-0.84, -2.38) * mm, "end": v(-0.7, -2.13) * mm});
            skPoint(sketch, "E203.visualSharp", {"position": v(-0.7, -0.83) * mm});
            skArc(sketch, "E203.filletArc", {"start": v(-0.7, -1.13) * mm, "mid": v(-0.79, -0.92) * mm, "end": v(-1, -0.83) * mm});
            skPoint(sketch, "E204.visualSharp", {"position": v(-2.52, -0.83) * mm});
            skArc(sketch, "E204.filletArc", {"start": v(-2.06, -0.83) * mm, "mid": v(-2.32, -0.98) * mm, "end": v(-2.32, -1.27) * mm});
            skPoint(sketch, "E205.visualSharp", {"position": v(-2.52, 0.81) * mm});
            skArc(sketch, "E205.filletArc", {"start": v(-2.33, 1.25) * mm, "mid": v(-2.33, 0.96) * mm, "end": v(-2.07, 0.81) * mm});
            skPoint(sketch, "E206.visualSharp", {"position": v(-0.7, 0.81) * mm});
            skArc(sketch, "E206.filletArc", {"start": v(-1, 0.81) * mm, "mid": v(-0.79, 0.9) * mm, "end": v(-0.7, 1.11) * mm});
            skPoint(sketch, "E207.visualSharp", {"position": v(-0.7, 2.56) * mm});
            skArc(sketch, "E207.filletArc", {"start": v(-0.7, 2.13) * mm, "mid": v(-0.84, 2.38) * mm, "end": v(-1.12, 2.4) * mm});
            skPoint(sketch, "E208.visualSharp", {"position": v(0.73, 0.81) * mm});
            skArc(sketch, "E208.filletArc", {"start": v(0.73, 1.11) * mm, "mid": v(0.82, 0.9) * mm, "end": v(1.03, 0.81) * mm});
            skPoint(sketch, "E209.visualSharp", {"position": v(0.73, 2.55) * mm});
            skArc(sketch, "E209.filletArc", {"start": v(1.16, 2.38) * mm, "mid": v(0.87, 2.37) * mm, "end": v(0.73, 2.11) * mm});
            skPoint(sketch, "E210.visualSharp", {"position": v(2.52, 0.81) * mm});
            skArc(sketch, "E210.filletArc", {"start": v(2.07, 0.81) * mm, "mid": v(2.33, 0.96) * mm, "end": v(2.33, 1.25) * mm});
            skSolve(sketch);
        }
        {
            var Q0;
            Q0 = qSketchRegion(id + "F14", true);
            var Q1;
            Q1=makeQuery(id+"F10.opExtrude","CAP_FACE",FACE,{"disambiguationData":[OSD([sQuery(id+"F8.wireOp",EDGE,"E31"),sQuery(id+"F8.wireOp",EDGE,"E32"),sQuery(id+"F8.wireOp",EDGE,"E33"),sQuery(id+"F8.wireOp",EDGE,"E34"),sQuery(id+"F8.wireOp",EDGE,"E35.filletArc"),sQuery(id+"F8.wireOp",EDGE,"E36.filletArc"),sQuery(id+"F8.wireOp",EDGE,"E37.filletArc"),sQuery(id+"F8.wireOp",EDGE,"E38.filletArc"),sQuery(id+"F8.wireOp",EDGE,"E43.0"),sQuery(id+"F8.wireOp",EDGE,"E43.1"),sQuery(id+"F8.wireOp",EDGE,"E43.2"),sQuery(id+"F8.wireOp",EDGE,"E43.3"),sQuery(id+"F8.wireOp",EDGE,"E44"),sQuery(id+"F8.wireOp",EDGE,"E47"),sQuery(id+"F8.wireOp",EDGE,"E48"),sQuery(id+"F8.wireOp",EDGE,"E51"),sQuery(id+"F8.wireOp",EDGE,"E52"),sQuery(id+"F8.wireOp",EDGE,"E55"),sQuery(id+"F8.wireOp",EDGE,"E56"),sQuery(id+"F8.wireOp",EDGE,"E59")])],"isStart":false});
            extrude(context, id + "F15", {"entities" : qUnion([Q0]), "operationType" : NewBodyOperationType.ADD, "depth" : 2 * mm, "endBoundEntityFace" : qUnion([Q1]), "offsetDistance" : 25 * mm});
        }
        {
            var Q0;
            Q0=makeQuery(id+"F1.opExtrude","CAP_FACE",FACE,{"disambiguationData":[OSD([sQuery(id+"F0.wireOp",EDGE,"E0"),sQuery(id+"F0.wireOp",EDGE,"E1"),sQuery(id+"F0.wireOp",EDGE,"E2"),sQuery(id+"F0.wireOp",EDGE,"E3")])],"isStart":false});
            var sketch = newSketch(context, id + "F16", { "sketchPlane" : qUnion([Q0])});
            skLineSegment(sketch, "E211.bottom", {"start": v(-8.43, 8.36) * mm, "end": v(8.4, 8.36) * mm});
            skLineSegment(sketch, "E211.top", {"start": v(-8.43, -8.61) * mm, "end": v(8.4, -8.61) * mm});
            skLineSegment(sketch, "E211.left", {"start": v(-8.43, 8.36) * mm, "end": v(-8.43, -8.61) * mm});
            skLineSegment(sketch, "E211.right", {"start": v(8.4, 8.36) * mm, "end": v(8.4, -8.61) * mm});
            skSolve(sketch);
        }
        {
            var Q0;
            Q0=makeQuery(id+"F1.opExtrude","CAP_FACE",FACE,{"disambiguationData":[OSD([sQuery(id+"F0.wireOp",EDGE,"E0"),sQuery(id+"F0.wireOp",EDGE,"E1"),sQuery(id+"F0.wireOp",EDGE,"E2"),sQuery(id+"F0.wireOp",EDGE,"E3")])],"isStart":true});
            var sketch = newSketch(context, id + "F17", { "sketchPlane" : qUnion([Q0])});
            skLineSegment(sketch, "E212", {"start": v(-9, 0) * mm, "end": v(-9, -2.5) * mm});
            skLineSegment(sketch, "E213", {"start": v(-9, 0) * mm, "end": v(-9, 2.5) * mm});
            skLineSegment(sketch, "E214", {"start": v(-9, 2.5) * mm, "end": v(-10.5, 2.5) * mm});
            skLineSegment(sketch, "E215", {"start": v(-9, 2.5) * mm, "end": v(-10.75, 2.5) * mm});
            skLineSegment(sketch, "E216", {"start": v(-10.75, 2.5) * mm, "end": v(-10.75, -2.5) * mm});
            skLineSegment(sketch, "E217", {"start": v(-10.75, -2.5) * mm, "end": v(-9, -2.5) * mm});
            skLineSegment(sketch, "E218", {"start": v(9, -2.5) * mm, "end": v(10.75, -2.5) * mm});
            skLineSegment(sketch, "E219", {"start": v(10.75, -2.5) * mm, "end": v(10.75, 2.5) * mm});
            skLineSegment(sketch, "E220", {"start": v(10.75, 2.5) * mm, "end": v(9, 2.5) * mm});
            skLineSegment(sketch, "E221", {"start": v(9, -2.5) * mm, "end": v(9, 2.5) * mm});
            skLineSegment(sketch, "E222", {"start": v(0, -9) * mm, "end": v(-2.5, -9) * mm});
            skLineSegment(sketch, "E223", {"start": v(-2.5, -9) * mm, "end": v(-2.5, -10.75) * mm});
            skLineSegment(sketch, "E224", {"start": v(-2.5, -10.75) * mm, "end": v(2.5, -10.75) * mm});
            skLineSegment(sketch, "E225", {"start": v(2.5, 9) * mm, "end": v(2.5, 10.75) * mm});
            skLineSegment(sketch, "E226", {"start": v(2.5, 10.75) * mm, "end": v(-2.5, 10.75) * mm});
            skLineSegment(sketch, "E227", {"start": v(-2.5, 10.75) * mm, "end": v(-2.5, 9) * mm});
            skLineSegment(sketch, "E228", {"start": v(2.5, 9) * mm, "end": v(-2.5, 9) * mm});
            skLineSegment(sketch, "E229", {"start": v(0, -9) * mm, "end": v(2.5, -9) * mm});
            skLineSegment(sketch, "E230", {"start": v(-6.25, -10.75) * mm, "end": v(-9.94, -10.75) * mm});
            skLineSegment(sketch, "E231", {"start": v(-10.75, -9.94) * mm, "end": v(-10.75, -6.25) * mm});
            skLineSegment(sketch, "E232", {"start": v(-8, -9) * mm, "end": v(-6.25, -9) * mm});
            skLineSegment(sketch, "E233", {"start": v(-6.25, -9) * mm, "end": v(-6.25, -10.75) * mm});
            skLineSegment(sketch, "E234", {"start": v(-9, -8) * mm, "end": v(-9, -6.25) * mm});
            skLineSegment(sketch, "E235", {"start": v(-9, -6.25) * mm, "end": v(-10.75, -6.25) * mm});
            skLineSegment(sketch, "E236", {"start": v(2.5, -10.75) * mm, "end": v(2.5, -9) * mm});
            skPoint(sketch, "E237.visualSharp", {"position": v(-10.75, -10.75) * mm});
            skArc(sketch, "E237.filletArc", {"start": v(-10.75, -9.94) * mm, "mid": v(-10.51, -10.51) * mm, "end": v(-9.94, -10.75) * mm});
            skLineSegment(sketch, "E238", {"start": v(-8, -9) * mm, "end": v(-8, -9) * mm});
            skLineSegment(sketch, "E239", {"start": v(-9, -8) * mm, "end": v(-9, -8) * mm});
            skPoint(sketch, "E240.visualSharp", {"position": v(-9, -9) * mm});
            skArc(sketch, "E240.filletArc", {"start": v(-9, -8) * mm, "mid": v(-8.7, -8.7) * mm, "end": v(-8, -9) * mm});
            skLineSegment(sketch, "E241.MirrorCS", {"start": v(6.25, -10.75) * mm, "end": v(9.94, -10.75) * mm});
            skArc(sketch, "E242.MirrorCS", {"start": v(10.75, -9.94) * mm, "mid": v(10.51, -10.51) * mm, "end": v(9.94, -10.75) * mm});
            skLineSegment(sketch, "E243.MirrorCS", {"start": v(10.75, -9.94) * mm, "end": v(10.75, -6.25) * mm});
            skLineSegment(sketch, "E244.MirrorCS", {"start": v(9, -6.25) * mm, "end": v(10.75, -6.25) * mm});
            skLineSegment(sketch, "E245.MirrorCS", {"start": v(9, -8) * mm, "end": v(9, -6.25) * mm});
            skArc(sketch, "E246.MirrorCS", {"start": v(9, -8) * mm, "mid": v(8.7, -8.7) * mm, "end": v(8, -9) * mm});
            skLineSegment(sketch, "E247.MirrorCS", {"start": v(6.25, -9) * mm, "end": v(6.25, -10.75) * mm});
            skLineSegment(sketch, "E248.MirrorCS", {"start": v(8, -9) * mm, "end": v(6.25, -9) * mm});
            skLineSegment(sketch, "E249.MirrorCS", {"start": v(6.25, 10.75) * mm, "end": v(9.94, 10.75) * mm});
            skArc(sketch, "E250.MirrorCS", {"start": v(10.75, 9.94) * mm, "mid": v(10.51, 10.51) * mm, "end": v(9.94, 10.75) * mm});
            skLineSegment(sketch, "E251.MirrorCS", {"start": v(10.75, 9.94) * mm, "end": v(10.75, 6.25) * mm});
            skLineSegment(sketch, "E252.MirrorCS", {"start": v(9, 6.25) * mm, "end": v(10.75, 6.25) * mm});
            skLineSegment(sketch, "E253.MirrorCS", {"start": v(9, 8) * mm, "end": v(9, 6.25) * mm});
            skArc(sketch, "E254.MirrorCS", {"start": v(9, 8) * mm, "mid": v(8.7, 8.7) * mm, "end": v(8, 9) * mm});
            skLineSegment(sketch, "E255.MirrorCS", {"start": v(8, 9) * mm, "end": v(6.25, 9) * mm});
            skLineSegment(sketch, "E256.MirrorCS", {"start": v(6.25, 9) * mm, "end": v(6.25, 10.75) * mm});
            skArc(sketch, "E257.MirrorCS", {"start": v(-10.75, 9.94) * mm, "mid": v(-10.51, 10.51) * mm, "end": v(-9.94, 10.75) * mm});
            skLineSegment(sketch, "E258.MirrorCS", {"start": v(-10.75, 9.94) * mm, "end": v(-10.75, 6.25) * mm});
            skLineSegment(sketch, "E259.MirrorCS", {"start": v(-9, 6.25) * mm, "end": v(-10.75, 6.25) * mm});
            skLineSegment(sketch, "E260.MirrorCS", {"start": v(-9, 8) * mm, "end": v(-9, 6.25) * mm});
            skArc(sketch, "E261.MirrorCS", {"start": v(-9, 8) * mm, "mid": v(-8.7, 8.7) * mm, "end": v(-8, 9) * mm});
            skLineSegment(sketch, "E262.MirrorCS", {"start": v(-8, 9) * mm, "end": v(-6.25, 9) * mm});
            skLineSegment(sketch, "E263.MirrorCS", {"start": v(-6.25, 10.75) * mm, "end": v(-9.94, 10.75) * mm});
            skLineSegment(sketch, "E264.MirrorCS", {"start": v(-6.25, 9) * mm, "end": v(-6.25, 10.75) * mm});
            skSolve(sketch);
        }
        {
            var Q0;
            Q0 = qSketchRegion(id + "F17", true);
            extrude(context, id + "F18", {"entities" : qUnion([Q0]), "operationType" : NewBodyOperationType.REMOVE, "depth" : 25 * mm, "offsetDistance" : 25 * mm});
        }
        {
            var Q0;
            Q0 = qSketchRegion(id + "F17", true);
            extrude(context, id + "F19", {"entities" : qUnion([Q0]), "operationType" : NewBodyOperationType.ADD, "depth" : 1 * mm, "offsetDistance" : 25 * mm});
        }
        {
            var Q0;
            {var subQ7=sQuery(id+"F4.wireOp",EDGE,"E25.0");Q0=makeQuery(id+"F7.boolean.opBoolean","SPLIT",FACE,{"disambiguationData":[TD([makeQuery(id+"F7.opExtrude","SWEPT_FACE",FACE,{"disambiguationData":[OSD([sQuery(id+"F2.wireOp",EDGE,"E4")])]})])],"derivedFrom":makeQuery(id+"F6.boolean.opBoolean","COPY",FACE,{"derivedFrom":makeQuery(id+"F6.opLoft","CAP_FACE",FACE,{"disambiguationData":[OSD([makeQuery(id+"F4.imprint","IMPRINT",FACE,{"disambiguationData":[TD([[makeQuery(id+"F4.imprint","IMPRINT",EDGE,{"derivedFrom":subQ7}),1.0]])]})])],"isStart":true})})});}
            var sketch = newSketch(context, id + "F20", { "sketchPlane" : qUnion([Q0])});
            skArc(sketch, "E265", {"start": v(-3.72, 4.34) * mm, "mid": v(-4.72, 2.65) * mm, "end": v(-3.02, 3.63) * mm});
            skArc(sketch, "E266.MirrorC", {"start": v(-2.85, 5.2) * mm, "mid": v(-1.15, 6.2) * mm, "end": v(-2.14, 4.5) * mm});
            skLineSegment(sketch, "E267", {"start": v(-2.58, 4.07) * mm, "end": v(-2.14, 4.5) * mm});
            skLineSegment(sketch, "E268", {"start": v(-2.58, 4.07) * mm, "end": v(-3.02, 3.63) * mm});
            skLineSegment(sketch, "E269", {"start": v(-3.29, 4.78) * mm, "end": v(-3.72, 4.34) * mm});
            skLineSegment(sketch, "E270", {"start": v(-3.29, 4.78) * mm, "end": v(-2.85, 5.2) * mm});
            skSolve(sketch);
        }
        {
            var Q0;
            Q0 = qSketchRegion(id + "F20", true);
            extrude(context, id + "F21", {"entities" : qUnion([Q0]), "operationType" : NewBodyOperationType.REMOVE, "oppositeDirection" : true, "depth" : 0.5 * mm, "offsetDistance" : 25 * mm});
        }
        {
            var Q0;
            Q0=makeQuery(id+"F1.opExtrude","SWEPT_BODY",BODY,{"disambiguationData":[OSD([sQuery(id+"F0.wireOp",EDGE,"E0"),sQuery(id+"F0.wireOp",EDGE,"E1"),sQuery(id+"F0.wireOp",EDGE,"E2"),sQuery(id+"F0.wireOp",EDGE,"E3")])]});
            var Q1;
            Q1=makeQuery(id+"F1.opExtrude","CAP_EDGE",EDGE,{"disambiguationData":[OSD([sQuery(id+"F0.wireOp",EDGE,"E1")])],"isStart":false});
            transform(context, id + "F22", {"entities" : qUnion([Q0]), "transformType" : TransformType.ROTATION, "transformAxis" : qUnion([Q1]), "angle" : 180 * degree, "makeCopy" : false});
        }
    });
